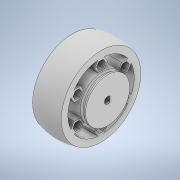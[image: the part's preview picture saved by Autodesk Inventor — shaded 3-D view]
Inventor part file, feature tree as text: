
AUTODESK INVENTOR PART (.ipt)
format: ipt  version: 2020 (Build 240168000, 168)  size: 288,768 bytes
history: native  units: in
note: dims shown in document units (in); Inventor stores cm internally (conversion verified against a paired STEP export)
features: sketch x4, extrude x2, revolve x2, projected_geometry x1
ambient origin geometry x8: Origin, YZ Plane, XZ Plane, XY Plane, X Axis, Y Axis, Z Axis, Center Point
bodies: Solid1 (feature_tree)
feature tree (9):
  extrude  "Extrusion1"  Depth=0.1181in
  sketch  "Sketch3"  dims[d6=0.7874in d7=0.1181in]
  revolve  "Revolution1"  [1 undecoded]
  extrude  "Extrusion2"  Depth=0.1181in
  revolve  "Revolution2"  [1 undecoded]
  sketch  "Sketch1"  dims[d0=0.1181in d1=0.0394in]
  sketch  "Sketch2"  dims[d3=1.4173in d4=0.1181in]
  projected_geometry  "Projected Loop1"
  sketch  "Sketch4"  dims[d8=0.0in d9=1.4173in d10=0.1181in d11=0.0315in d12=2.3622in d14=360.0deg d16=0.5118in d17=0.0in d19=90.0deg d20=0.0394in d22=60.0deg d23=60.0deg d24=0.0394in d25=90.0deg]
note: 2 required parameter values undecoded (feature->parameter linkage not recoverable at this tier; creation-order binding heuristic only, values carry confidence <= 0.55)
